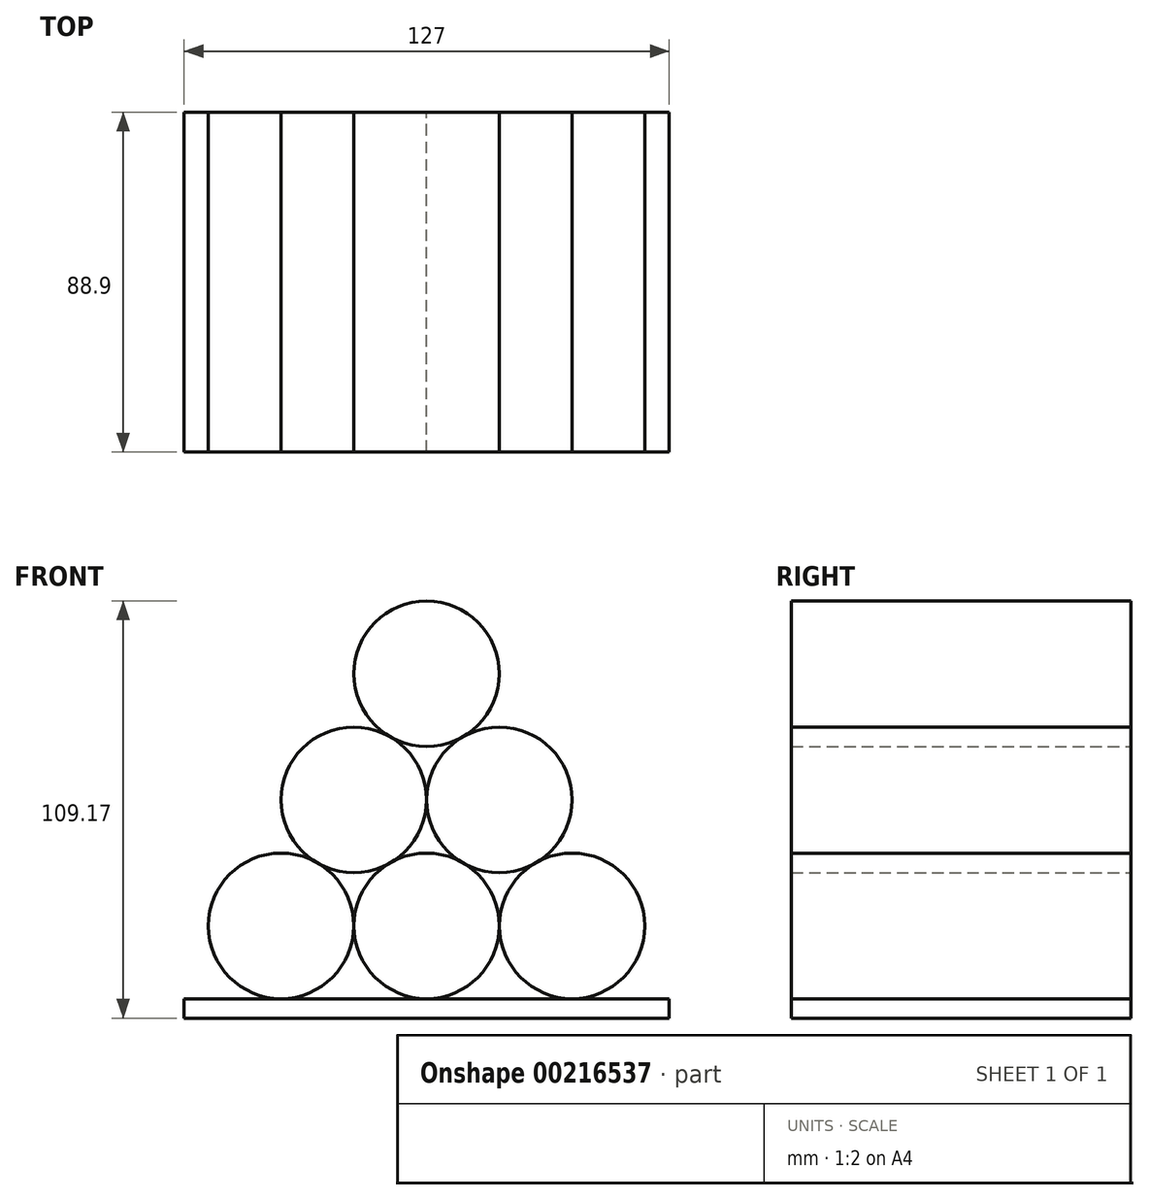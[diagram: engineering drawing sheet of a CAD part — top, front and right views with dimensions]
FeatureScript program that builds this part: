
annotation { "Feature Type Name" : "Feature", "Feature Type Description" : "" }
export const myFeature = defineFeature(function(context is Context, id is Id, definition is map)
    precondition{}
    {
        {
            var Q0;
            Q0=qCreatedBy(makeId("Front.planeOp"),FACE);
            var sketch = newSketch(context, id + "F0", { "sketchPlane" : qUnion([Q0])});
            skCircle(sketch, "E0", {"center": v(-19.11, 6.18) * mm, "radius": 19.05 * mm});
            skCircle(sketch, "E1", {"center": v(18.99, 6.18) * mm, "radius": 19.05 * mm});
            skCircle(sketch, "E2", {"center": v(-38.16, -26.82) * mm, "radius": 19.05 * mm});
            skCircle(sketch, "E3", {"center": v(-0.06, -26.82) * mm, "radius": 19.05 * mm});
            skCircle(sketch, "E4", {"center": v(38.04, -26.82) * mm, "radius": 19.05 * mm});
            skLineSegment(sketch, "E5", {"start": v(38.04, -26.82) * mm, "end": v(-48.43, -26.82) * mm, "construction": true});
            skLineSegment(sketch, "E6.bottom", {"start": v(-63.5, -45.87) * mm, "end": v(63.5, -45.87) * mm});
            skLineSegment(sketch, "E6.top", {"start": v(-63.5, -50.95) * mm, "end": v(63.5, -50.95) * mm});
            skLineSegment(sketch, "E6.left", {"start": v(-63.5, -45.87) * mm, "end": v(-63.5, -50.95) * mm});
            skLineSegment(sketch, "E6.right", {"start": v(63.5, -45.87) * mm, "end": v(63.5, -50.95) * mm});
            skCircle(sketch, "E7", {"center": v(-0.06, 39.17) * mm, "radius": 19.05 * mm});
            skSolve(sketch);
        }
        {
            var Q0;
            {var subQ0=sQuery(id+"F0.wireOp",EDGE,"E0");var subQ1=makeQuery(id+"F0.imprint","INTERSECT",VERTEX,{"derivedFrom":[subQ0,sQuery(id+"F0.wireOp",EDGE,"E2")]});Q0=makeQuery(id+"F0.imprint","IMPRINT",FACE,{"disambiguationData":[TD([[makeQuery(id+"F0.imprint","IMPRINT",EDGE,{"disambiguationData":[TD([[subQ1,1.0]])],"derivedFrom":subQ0}),1.0]])]});}
            var Q1;
            {var subQ0=sQuery(id+"F0.wireOp",EDGE,"E1");var subQ1=makeQuery(id+"F0.imprint","INTERSECT",VERTEX,{"derivedFrom":[sQuery(id+"F0.wireOp",EDGE,"E0"),subQ0]});Q1=makeQuery(id+"F0.imprint","IMPRINT",FACE,{"disambiguationData":[TD([[makeQuery(id+"F0.imprint","IMPRINT",EDGE,{"disambiguationData":[TD([[subQ1,-1.0]])],"derivedFrom":subQ0}),1.0]])]});}
            var Q2;
            {var subQ0=sQuery(id+"F0.wireOp",EDGE,"E3");var subQ4=makeQuery(id+"F0.imprint","INTERSECT",VERTEX,{"derivedFrom":[sQuery(id+"F0.wireOp",EDGE,"E1"),subQ0]});Q2=makeQuery(id+"F0.imprint","IMPRINT",FACE,{"disambiguationData":[TD([[makeQuery(id+"F0.imprint","IMPRINT",EDGE,{"disambiguationData":[TD([[subQ4,1.0]])],"derivedFrom":subQ0}),1.0]])]});}
            var Q3;
            {var subQ0=sQuery(id+"F0.wireOp",EDGE,"E4");var subQ1=makeQuery(id+"F0.imprint","INTERSECT",VERTEX,{"derivedFrom":[sQuery(id+"F0.wireOp",EDGE,"E1"),subQ0]});Q3=makeQuery(id+"F0.imprint","IMPRINT",FACE,{"disambiguationData":[TD([[makeQuery(id+"F0.imprint","IMPRINT",EDGE,{"disambiguationData":[TD([[subQ1,-1.0]])],"derivedFrom":subQ0}),1.0]])]});}
            var Q4;
            {var subQ0=sQuery(id+"F0.wireOp",EDGE,"E2");var subQ1=makeQuery(id+"F0.imprint","INTERSECT",VERTEX,{"derivedFrom":[sQuery(id+"F0.wireOp",EDGE,"E0"),subQ0]});Q4=makeQuery(id+"F0.imprint","IMPRINT",FACE,{"disambiguationData":[TD([[makeQuery(id+"F0.imprint","IMPRINT",EDGE,{"disambiguationData":[TD([[subQ1,1.0]])],"derivedFrom":subQ0}),1.0]])]});}
            var Q5;
            Q5=makeQuery(id+"F0.imprint","IMPRINT",FACE,{"disambiguationData":[TD([[makeQuery(id+"F0.imprint","IMPRINT",EDGE,{"derivedFrom":sQuery(id+"F0.wireOp",EDGE,"E6.top")}),1.0]])]});
            var Q6;
            {var subQ0=sQuery(id+"F0.wireOp",EDGE,"E7");var subQ1=makeQuery(id+"F0.imprint","INTERSECT",VERTEX,{"derivedFrom":[sQuery(id+"F0.wireOp",EDGE,"E0"),subQ0]});Q6=makeQuery(id+"F0.imprint","IMPRINT",FACE,{"disambiguationData":[TD([[makeQuery(id+"F0.imprint","IMPRINT",EDGE,{"disambiguationData":[TD([[subQ1,-1.0]])],"derivedFrom":subQ0}),1.0]])]});}
            var Q7;
            Q7=sQuery(id+"F0.wireOp",EDGE,"E0");
            var Q8;
            Q8=sQuery(id+"F0.wireOp",EDGE,"E1");
            var Q9;
            Q9=sQuery(id+"F0.wireOp",EDGE,"E2");
            var Q10;
            Q10=sQuery(id+"F0.wireOp",EDGE,"E3");
            var Q11;
            Q11=sQuery(id+"F0.wireOp",EDGE,"E4");
            var Q12;
            Q12=sQuery(id+"F0.wireOp",EDGE,"E6.bottom");
            var Q13;
            Q13=sQuery(id+"F0.wireOp",EDGE,"E6.top");
            var Q14;
            Q14=sQuery(id+"F0.wireOp",EDGE,"E6.left");
            var Q15;
            Q15=sQuery(id+"F0.wireOp",EDGE,"E6.right");
            extrude(context, id + "F1", {"entities" : qUnion([Q0, Q1, Q2, Q3, Q4, Q5, Q6]), "surfaceEntities" : qUnion([Q7, Q8, Q9, Q10, Q11, Q12, Q13, Q14, Q15]), "depth" : 88.9 * mm});
        }
    });
